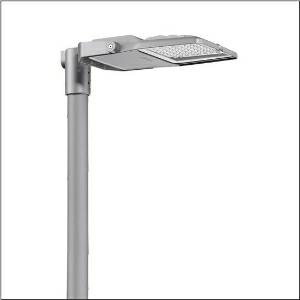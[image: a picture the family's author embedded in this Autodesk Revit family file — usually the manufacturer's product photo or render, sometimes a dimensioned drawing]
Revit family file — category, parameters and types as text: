
# Revit family: floodlight_fl_21_iq_mini___pl61_5xa7771c4c3a_1011
name_source: partatom
category: Lighting Fixtures
units: mm (PartAtom-declared; Revit-internal decimal feet)

## family parameters
Cut with Voids When Loaded = No
Host = Face
Light Source = No
Part Type = Normal
Room Calculation Point = No
Round Connector Dimension = Use Diameter
Shared = No

## types (1)
- --- (1 x LED, 12490 lm, 87.2 W, 4000K)
    Apparent Load = 87 VA
    CIE Flux Codes = 33 65 98 100 100
    Color Rendering = 70
    Color Temperature = 4000K
    Default Elevation = 1800 mm
    Description = Floodlight FL 21 iQ mini, floodlight, primary light control with lens, of PMMA, primary optical cover: protective disc, of toughened safety glass, transparent, light distribution: PL61, light emission: direct distribution, installation type: surface-mounted, LED, High Power LED, rated luminous flux: 12.490lm, luminous efficacy: 143lm/W, light colour: 740, colour temperature: 4000K, control gear: iQ Comfort/DALI, control: Auto-Match, Temp-Guard, Lumen-Switch, Night-Set, Smart-Wire, Light-Fading, Desk-Remote (wireless, voltage-free reading and setting of iQ features in the workshop via application-optimized NFC function/RFID function), optimised constant luminous flux control (CLO 2.0), with terminal, 6-pole, mains connection: 220..240V, AC, 50/60Hz, start of lifetime: 87W, end of service life: 92W, reduction: 40W, luminaire housing, of diecast aluminium, powder-coated, Siteco® metallic grey (DB 702S), corrosivity category C5 mid according to DIN EN ISO 12944, suitable for swimming pools, chlorine-resistant, sealing non-destructively replaceable, please order mast flange separately, mast bracket, of steel, galvanised, powder-coated, Siteco® metallic grey (DB 702S), protection rating (complete): IP66, insulation class (complete): insulation class II (safety insulation), certification: CE, ENEC, VDE, protection symbol: D, impact resistance: IK08, permissible operating ambient temperature: -40..+40°C, permissible operating ambient temperature for outdoor applications: -40..+50°C, standard: DIN EN 12944, LABS conformity tested according to VDMA 24364:2018-05, packaging unit: 1 piece

Light Distribution: PL61
    Height = 70 mm
    Lamp = 1 x LED
    Lamp Light Flux = 12490 lm
    Lamp Power = 87.2 W
    Lamp count = 1
    Length = 485 mm
    Luminous efficacy = 143 lm/W
    Manufacturer = Siteco
    ModVariant = No
    Model = 5XA7771C4C3A
    Number of Poles = 1
    OnlyDefault = Yes
    Power Factor = 1
    Product Name = Floodlight FL 21 iQ mini | PL61
    Product group = floodlight | pylon annexe
    ProductGroupID = 6200
    Protection Class = Protection class II
    Protection Degree = IP 66
    RLX_Detail_Level = 1
    RLX_Emergency_Light_Flux = 0 lm
    RLX_Emergency_Type = 0
    RLX_Emergency_Type_DB = No
    RlxData = <blob elided: 101497 chars, md5=a373c1c1>
    Socket = socket
    Standby Power = 0 W
    System Light Flux = 12490 lm
    System Power = 87 W
    Type Comments = factory setting: luminous flux: 100 % | dim-lin: 254 | 456 mA
    Type Image = l_1007125.jpg
    URL = http://relux.com
    VarID = @adj_173188
    Voltage = 0 V
    Weight = 0.00 kg
    Width = 337 mm

## geometry (parser evidence)
native form markers: Blend x4, Sweep x13
no freeform markers — native parametric forms only
